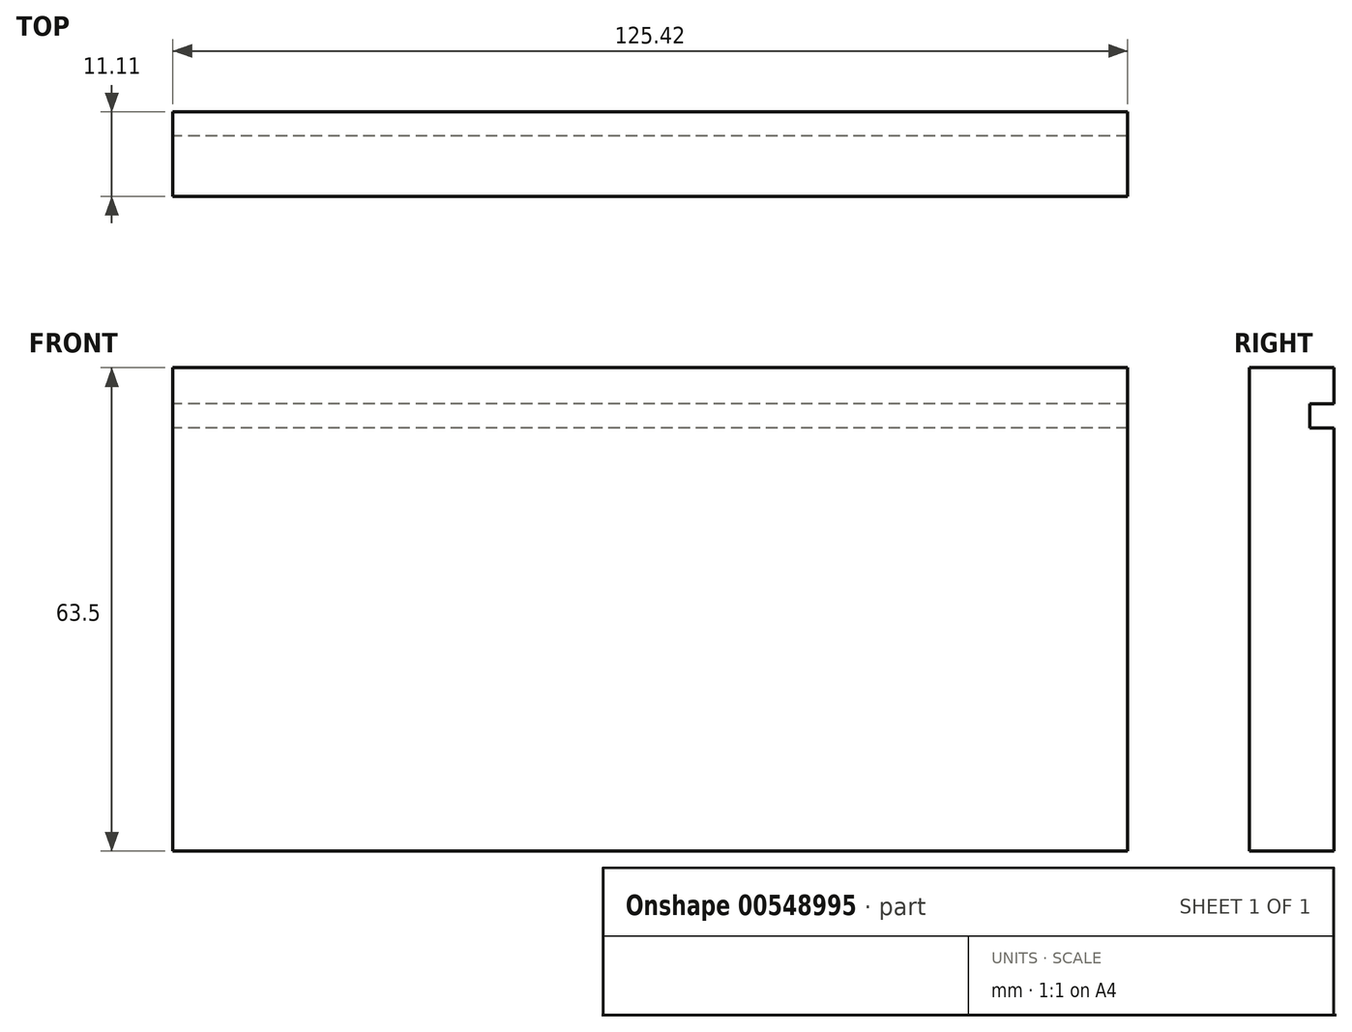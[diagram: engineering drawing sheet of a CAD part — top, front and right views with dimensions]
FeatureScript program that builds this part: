
annotation { "Feature Type Name" : "Feature", "Feature Type Description" : "" }
export const myFeature = defineFeature(function(context is Context, id is Id, definition is map)
    precondition{}
    {
        {
            var Q0;
            Q0=qCreatedBy(makeId("Front.planeOp"),FACE);
            var sketch = newSketch(context, id + "F0", { "sketchPlane" : qUnion([Q0])});
            skLineSegment(sketch, "E0.bottom", {"start": v(62.7, -31.75) * mm, "end": v(-62.7, -31.75) * mm});
            skLineSegment(sketch, "E0.top", {"start": v(62.7, 31.75) * mm, "end": v(-62.7, 31.75) * mm});
            skLineSegment(sketch, "E0.left", {"start": v(62.7, -31.75) * mm, "end": v(62.7, 31.75) * mm});
            skLineSegment(sketch, "E0.right", {"start": v(-62.7, -31.75) * mm, "end": v(-62.7, 31.75) * mm});
            skPoint(sketch, "E0.middle", {"position": v(0, 0) * mm});
            skSolve(sketch);
        }
        {
            var Q0;
            Q0 = qSketchRegion(id + "F0", true);
            extrude(context, id + "F1", {"entities" : qUnion([Q0]), "depth" : 11.1 * mm, "offsetDistance" : 25.4 * mm});
        }
        {
            var Q0;
            Q0=makeQuery(id+"F1.opExtrude","CAP_FACE",FACE,{"disambiguationData":[OSD([sQuery(id+"F0.wireOp",EDGE,"E0.bottom"),sQuery(id+"F0.wireOp",EDGE,"E0.top"),sQuery(id+"F0.wireOp",EDGE,"E0.left"),sQuery(id+"F0.wireOp",EDGE,"E0.right")])],"isStart":true});
            var sketch = newSketch(context, id + "F2", { "sketchPlane" : qUnion([Q0])});
            skLineSegment(sketch, "E1.bottom", {"start": v(-62.7, 26.99) * mm, "end": v(62.7, 26.99) * mm});
            skLineSegment(sketch, "E1.top", {"start": v(-62.7, 23.81) * mm, "end": v(62.7, 23.81) * mm});
            skLineSegment(sketch, "E1.left", {"start": v(-62.7, 26.99) * mm, "end": v(-62.7, 23.81) * mm});
            skLineSegment(sketch, "E1.right", {"start": v(62.7, 23.81) * mm, "end": v(62.7, 26.99) * mm});
            skSolve(sketch);
        }
        {
            var Q0;
            Q0 = qSketchRegion(id + "F2", true);
            extrude(context, id + "F3", {"entities" : qUnion([Q0]), "operationType" : NewBodyOperationType.REMOVE, "oppositeDirection" : true, "depth" : 3.17 * mm, "offsetDistance" : 25.4 * mm});
        }
    });
